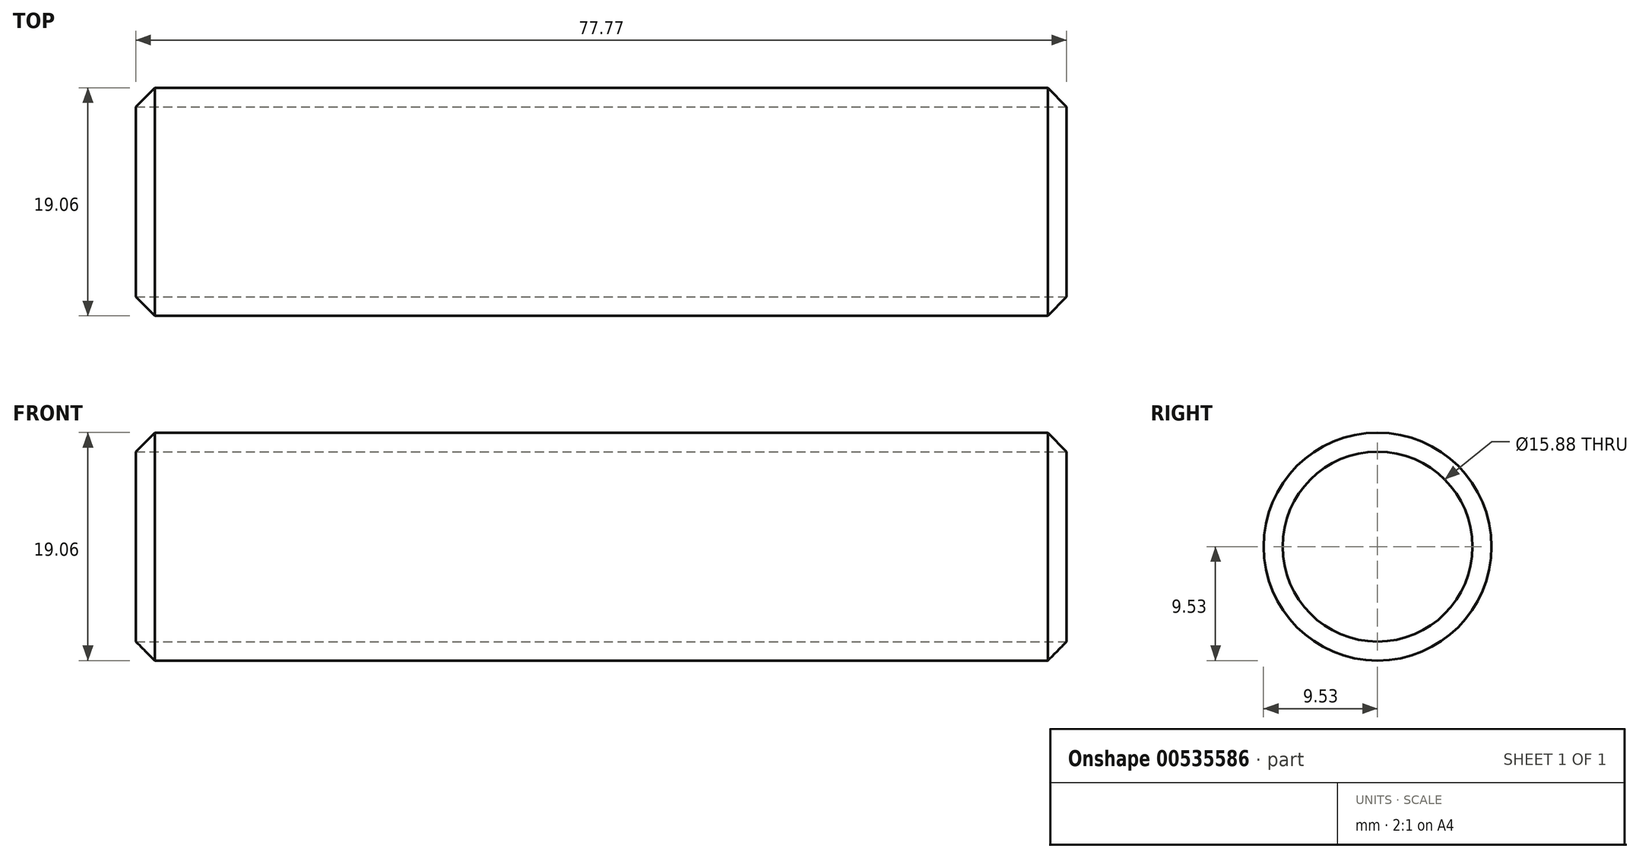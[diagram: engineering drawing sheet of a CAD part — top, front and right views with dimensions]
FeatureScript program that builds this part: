
annotation { "Feature Type Name" : "Feature", "Feature Type Description" : "" }
export const myFeature = defineFeature(function(context is Context, id is Id, definition is map)
    precondition{}
    {
        {
            var Q0;
            Q0=qCreatedBy(makeId("Top.planeOp"),FACE);
            var sketch = newSketch(context, id + "F0", { "sketchPlane" : qUnion([Q0])});
            skLineSegment(sketch, "E0.bottom", {"start": v(0, 7.94) * mm, "end": v(-77.77, 7.94) * mm});
            skLineSegment(sketch, "E0.top", {"start": v(-1.57, 9.53) * mm, "end": v(-76.2, 9.52) * mm});
            skLineSegment(sketch, "E1", {"start": v(0, 0) * mm, "end": v(-73.56, 0) * mm, "construction": true});
            skPoint(sketch, "E2.visualSharp", {"position": v(-77.77, 9.52) * mm});
            skLineSegment(sketch, "E3", {"start": v(-77.77, 7.94) * mm, "end": v(-76.2, 9.53) * mm});
            skPoint(sketch, "E4.visualSharp", {"position": v(0, 9.53) * mm});
            skLineSegment(sketch, "E5", {"start": v(0, 7.94) * mm, "end": v(-1.57, 9.53) * mm});
            skSolve(sketch);
        }
        {
            var Q0;
            Q0 = qSketchRegion(id + "F0", true);
            var Q1;
            Q1=sQuery(id+"F0.wireOp",EDGE,"E1");
            revolve(context, id + "F1", {"entities" : qUnion([Q0]), "axis" : qUnion([Q1]), "revolveType" : RevolveType.FULL});
        }
    });
